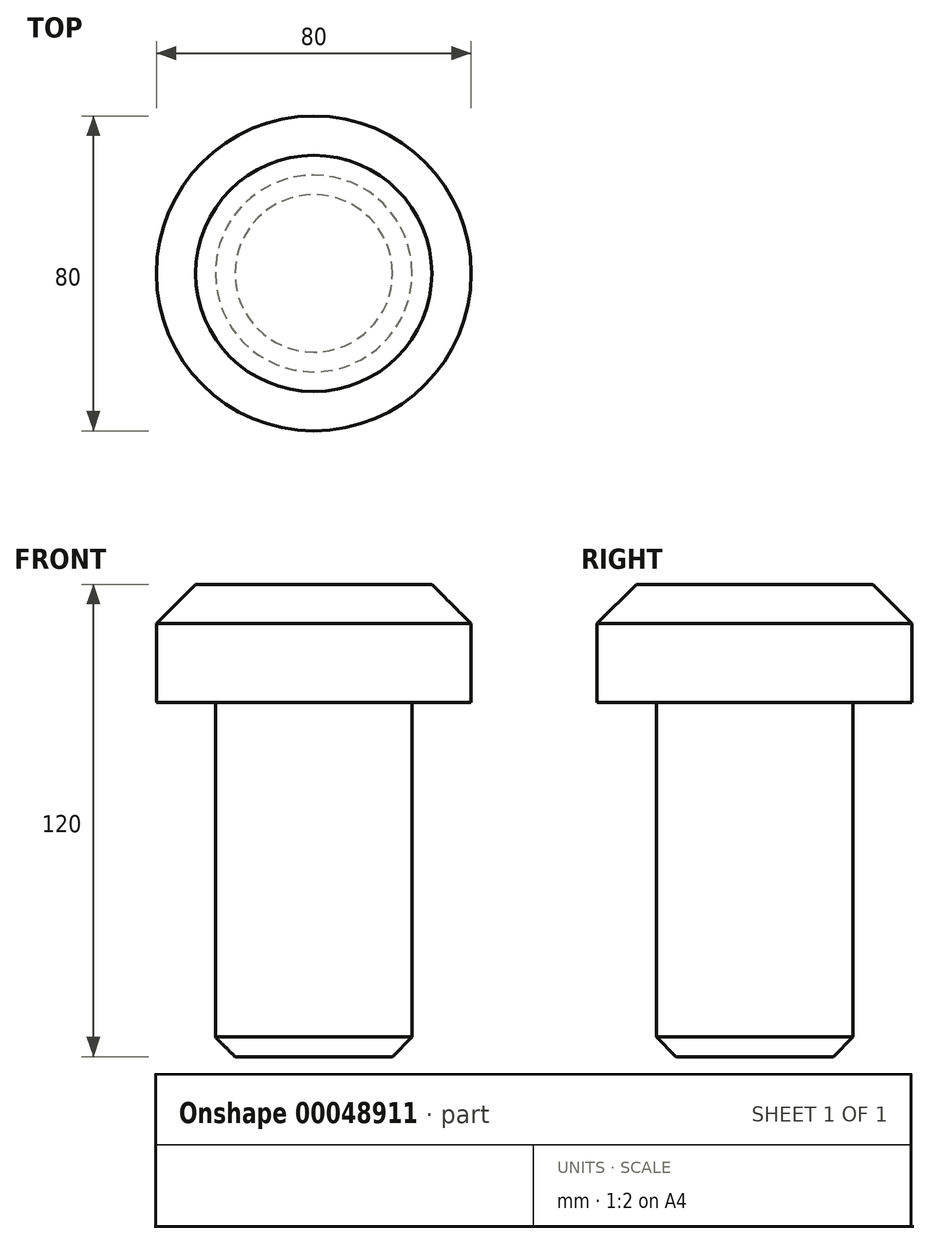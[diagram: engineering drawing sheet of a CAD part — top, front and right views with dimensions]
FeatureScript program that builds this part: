
annotation { "Feature Type Name" : "Feature", "Feature Type Description" : "" }
export const myFeature = defineFeature(function(context is Context, id is Id, definition is map)
    precondition{}
    {
        {
            var Q0;
            Q0=qCreatedBy(makeId("Top.planeOp"),FACE);
            var sketch = newSketch(context, id + "F0", { "sketchPlane" : qUnion([Q0])});
            skCircle(sketch, "E0", {"center": v(0, 0) * mm, "radius": 40 * mm});
            skSolve(sketch);
        }
        {
            var Q0;
            Q0 = qSketchRegion(id + "F0", true);
            extrude(context, id + "F1", {"entities" : qUnion([Q0]), "depth" : 10 * mm});
        }
        {
            var Q0;
            Q0=makeQuery(id+"F1.opExtrude","CAP_FACE",FACE,{"disambiguationData":[OSD([sQuery(id+"F0.wireOp",EDGE,"E0")])],"isStart":true});
            var sketch = newSketch(context, id + "F2", { "sketchPlane" : qUnion([Q0])});
            skCircle(sketch, "E1", {"center": v(0, 0) * mm, "radius": 40 * mm});
            skSolve(sketch);
        }
        {
            var Q0;
            Q0=makeQuery(id+"F1.opExtrude","CAP_EDGE",EDGE,{"disambiguationData":[OSD([sQuery(id+"F0.wireOp",EDGE,"E0")])],"isStart":false});
            chamfer(context, id + "F3", {"entities" : qUnion([Q0]), "width" : 10 * mm, "tangentPropagation" : true});
        }
        {
            var Q0;
            Q0 = qSketchRegion(id + "F2", true);
            extrude(context, id + "F4", {"entities" : qUnion([Q0]), "operationType" : NewBodyOperationType.ADD, "depth" : 20 * mm});
        }
        {
            var Q0;
            Q0=makeQuery(id+"F4.opExtrude","CAP_FACE",FACE,{"disambiguationData":[OSD([sQuery(id+"F2.wireOp",EDGE,"E1")])],"isStart":false});
            var sketch = newSketch(context, id + "F5", { "sketchPlane" : qUnion([Q0])});
            skCircle(sketch, "E2", {"center": v(0, 0) * mm, "radius": 25 * mm});
            skSolve(sketch);
        }
        {
            var Q0;
            Q0=makeQuery(id+"F5.imprint","IMPRINT",FACE,{"disambiguationData":[TD([[makeQuery(id+"F5.imprint","IMPRINT",EDGE,{"derivedFrom":sQuery(id+"F5.wireOp",EDGE,"E2")}),1.0]])]});
            extrude(context, id + "F6", {"entities" : qUnion([Q0]), "operationType" : NewBodyOperationType.ADD, "depth" : 90 * mm});
        }
        {
            var Q0;
            Q0=makeQuery(id+"F6.opExtrude","CAP_EDGE",EDGE,{"disambiguationData":[OSD([sQuery(id+"F5.wireOp",EDGE,"E2")])],"isStart":false});
            chamfer(context, id + "F7", {"entities" : qUnion([Q0]), "width" : 5 * mm, "tangentPropagation" : true});
        }
    });
